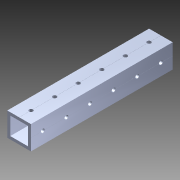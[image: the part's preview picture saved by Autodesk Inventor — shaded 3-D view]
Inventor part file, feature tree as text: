
AUTODESK INVENTOR PART (.ipt)
format: ipt  version: 2014 SP1 (Build 180222100, 222)  size: 1,135,104 bytes
history: native  units: in
note: dims shown in document units (in); Inventor stores cm internally (conversion verified against a paired STEP export)
features: pattern_circular x1, other x1, plane x1, extrude x1, imported_body x1, sketch x1
ambient origin geometry x8: Origin, YZ Plane, XZ Plane, XY Plane, X Axis, Y Axis, Z Axis, Center Point
bodies: Body1 (feature_tree)
feature tree (6):
  pattern_circular  "CirPattern2"
  other  "217-3426-STEP1"
  plane  "Work Plane1"
  extrude  "Extrusion1"  Depth=3937.0079in TaperAngle=0.0deg
  imported_body  "Base1"
  sketch  "Sketch1"  dims[d0=-6.0in d1=3937.0079in d2=0.0in]
